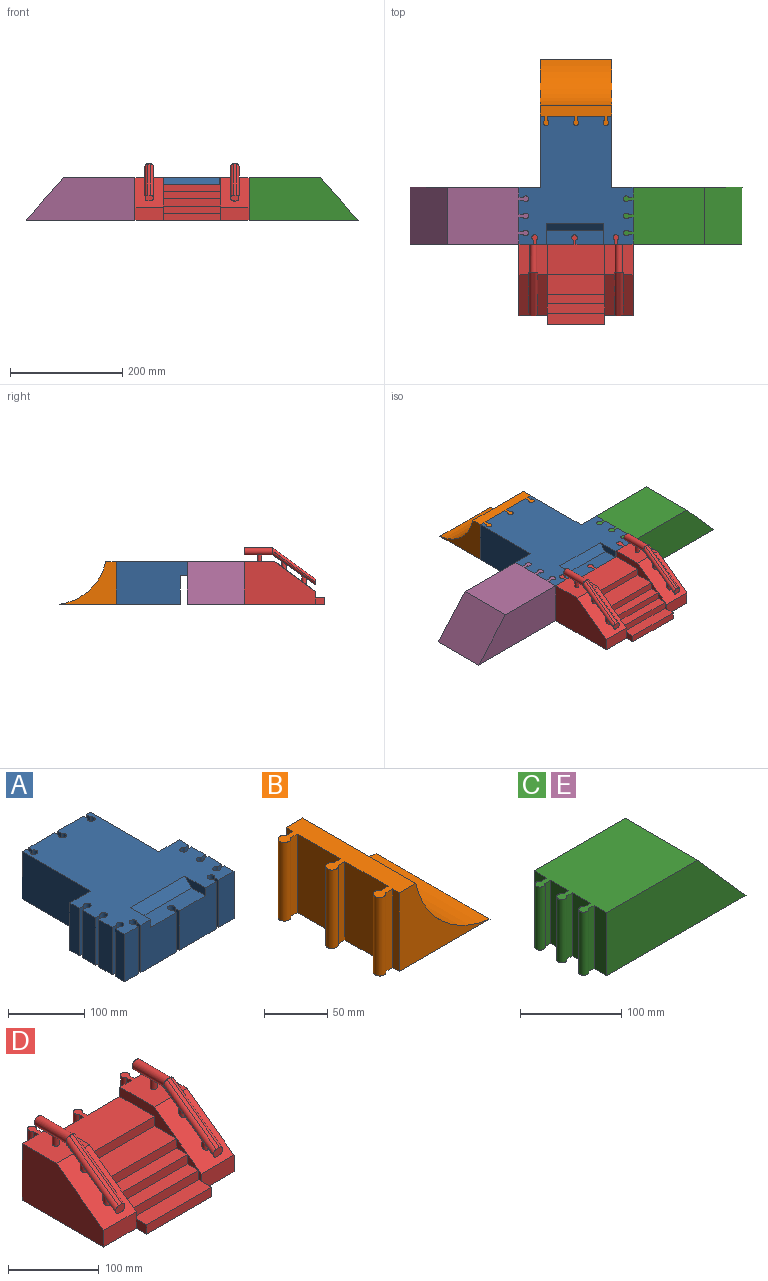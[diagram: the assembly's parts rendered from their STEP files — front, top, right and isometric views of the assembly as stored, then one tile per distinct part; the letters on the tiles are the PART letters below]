
ASSEMBLY  parts=5 mates=4
PART A: 72 faces, bbox 203.2x228.6x76.2 mm
  f0: plane 76.2x68.58mm, normal (0,-1,0), area 4612.9mm2, adj f1,f10,f18,f37,f69,f70
  f1: plane 63.5x7.62mm, normal (-1,0,0), area 483.9mm2, adj f0,f3,f10,f70
  f2: plane 63.5x7.62mm, normal (1,0,0), area 483.9mm2, adj f3,f10,f14,f70
  f3: cylinder r=5.08mm len=63.5mm, axis (0,0,-1), area 1689mm2, adj f1,f2,f10,f70
  f4: plane 76.2x25.4mm, normal (-1,0,0), area 1935.5mm2, adj f10,f18,f53,f57
  f5: plane 76.2x25.4mm, normal (-1,0,0), area 1935.5mm2, adj f10,f18,f50,f54
  f6: plane 76.2x17.78mm, normal (-1,0,0), area 1354.8mm2, adj f10,f11,f18,f51
  f7: plane 76.2x17.78mm, normal (1,0,0), area 1354.8mm2, adj f10,f18,f22,f67
  f8: plane 76.2x25.4mm, normal (1,0,0), area 1935.5mm2, adj f10,f18,f64,f65
  f9: plane 76.2x25.4mm, normal (1,0,0), area 1935.5mm2, adj f10,f18,f61,f62
  f10: plane 203.2x101.6mm, normal (0,0,-1), area 9910.7mm2, adj f0,f1,f2,f3,f4,f5,f6,f7
  f11: plane 76.2x38.1mm, normal (0,1,0), area 2258.1mm2, adj f6,f10,f18,f25,f48,f49
  f12: plane 127x114.3mm, normal (0,0,-1), area 6421.8mm2, adj f15,f16,f17,f23,f24,f25,f26,f27
  f13: plane 76.2x25.4mm, normal (0,-1,0), area 1935.5mm2, adj f10,f18,f19,f40
  f14: plane 76.2x66.04mm, normal (0,-1,0), area 4419.3mm2, adj f2,f10,f18,f39,f68,f70
  f15: plane 76.2x48.26mm, normal (0,1,0), area 3677.4mm2, adj f12,f18,f31,f33
  f16: plane 76.2x48.26mm, normal (0,1,0), area 3677.4mm2, adj f12,f18,f26,f30
  f17: plane 76.2x7.62mm, normal (0,1,0), area 580.6mm2, adj f12,f18,f25,f28
  f18: plane 228.6x203.2mm, normal (0,0,1), area 31611.3mm2, adj f0,f4,f5,f6,f7,f8,f9,f11
  f19: plane 76.2x17.78mm, normal (-1,0,0), area 1354.8mm2, adj f10,f13,f18,f56
  f20: plane 76.2x27.94mm, normal (0,-1,0), area 2129mm2, adj f10,f18,f21,f36
  f21: plane 76.2x17.78mm, normal (1,0,0), area 1354.8mm2, adj f10,f18,f20,f59
  f22: plane 76.2x38.1mm, normal (0,1,0), area 2258.1mm2, adj f7,f10,f18,f23,f46,f49
  f23: plane 127x76.2mm, normal (1,0,0), area 9032.2mm2, adj f12,f18,f22,f24,f45,f49
  f24: plane 76.2x7.62mm, normal (0,1,0), area 580.6mm2, adj f12,f18,f23,f34
  f25: plane 127x76.2mm, normal (-1,0,0), area 9032.2mm2, adj f11,f12,f17,f18,f41,f49
  f26: plane 76.2x7.62mm, normal (-1,0,0), area 580.6mm2, adj f12,f16,f18,f27
  f27: cylinder r=5.08mm len=76.2mm, axis (0,0,-1), area 2026.8mm2, adj f12,f18,f26,f28
  f28: plane 76.2x7.62mm, normal (1,0,0), area 580.6mm2, adj f12,f17,f18,f27
  f29: cylinder r=5.08mm len=76.2mm, axis (0,0,-1), area 2026.8mm2, adj f12,f18,f30,f31
  f30: plane 76.2x7.62mm, normal (1,0,0), area 580.6mm2, adj f12,f16,f18,f29
  f31: plane 76.2x7.62mm, normal (-1,0,0), area 580.6mm2, adj f12,f15,f18,f29
  f32: cylinder r=5.08mm len=76.2mm, axis (0,0,-1), area 2026.8mm2, adj f12,f18,f33,f34
  f33: plane 76.2x7.62mm, normal (1,0,0), area 580.6mm2, adj f12,f15,f18,f32
  f34: plane 76.2x7.62mm, normal (-1,0,0), area 580.6mm2, adj f12,f18,f24,f32
  f35: cylinder r=5.08mm len=76.2mm, axis (0,0,-1), area 2026.8mm2, adj f10,f18,f36,f37
  f36: plane 76.2x7.62mm, normal (-1,0,0), area 580.6mm2, adj f10,f18,f20,f35
  f37: plane 76.2x7.62mm, normal (1,0,0), area 580.6mm2, adj f0,f10,f18,f35
  f38: cylinder r=5.08mm len=76.2mm, axis (0,0,-1), area 2026.8mm2, adj f10,f18,f39,f40
  f39: plane 76.2x7.62mm, normal (-1,0,0), area 580.6mm2, adj f10,f14,f18,f38
  f40: plane 76.2x7.62mm, normal (1,0,0), area 580.6mm2, adj f10,f13,f18,f38
  f41: plane 50.8x12.7mm, normal (0,-1,0), area 645.2mm2, adj f12,f25,f42,f49
  f42: plane 76.2x50.8mm, normal (1,0,0), area 3871mm2, adj f12,f41,f43,f49
  f43: plane 101.6x50.8mm, normal (0,-1,0), area 5161.3mm2, adj f12,f42,f44,f49
  f44: plane 76.2x50.8mm, normal (-1,0,0), area 3871mm2, adj f12,f43,f45,f49
  f45: plane 50.8x12.7mm, normal (0,-1,0), area 645.2mm2, adj f12,f23,f44,f49
  f46: plane 63.5x50.8mm, normal (-1,0,0), area 3225.8mm2, adj f10,f22,f47,f49
  f47: plane 152.4x50.8mm, normal (0,1,0), area 7741.9mm2, adj f10,f46,f48,f49
  f48: plane 63.5x50.8mm, normal (1,0,0), area 3225.8mm2, adj f10,f11,f47,f49
  f49: plane 152.4x152.4mm, normal (0,0,-1), area 19032.2mm2, adj f11,f22,f23,f25,f41,f42,f43,f44
  f50: plane 76.2x7.62mm, normal (0,1,0), area 580.6mm2, adj f5,f10,f18,f52
  f51: plane 76.2x7.62mm, normal (0,-1,0), area 580.6mm2, adj f6,f10,f18,f52
  f52: cylinder r=5.08mm len=76.2mm, axis (0,0,-1), area 2026.8mm2, adj f10,f18,f50,f51
  f53: plane 76.2x7.62mm, normal (0,1,0), area 580.6mm2, adj f4,f10,f18,f55
  f54: plane 76.2x7.62mm, normal (0,-1,0), area 580.6mm2, adj f5,f10,f18,f55
  f55: cylinder r=5.08mm len=76.2mm, axis (0,0,-1), area 2026.8mm2, adj f10,f18,f53,f54
  f56: plane 76.2x7.62mm, normal (0,1,0), area 580.6mm2, adj f10,f18,f19,f58
  f57: plane 76.2x7.62mm, normal (0,-1,0), area 580.6mm2, adj f4,f10,f18,f58
  f58: cylinder r=5.08mm len=76.2mm, axis (0,0,-1), area 2026.8mm2, adj f10,f18,f56,f57
  f59: plane 76.2x7.62mm, normal (0,1,0), area 580.6mm2, adj f10,f18,f21,f60
  f60: cylinder r=5.08mm len=76.2mm, axis (0,0,-1), area 2026.8mm2, adj f10,f18,f59,f61
  f61: plane 76.2x7.62mm, normal (0,-1,0), area 580.6mm2, adj f9,f10,f18,f60
  f62: plane 76.2x7.62mm, normal (0,1,0), area 580.6mm2, adj f9,f10,f18,f63
  f63: cylinder r=5.08mm len=76.2mm, axis (0,0,-1), area 2026.8mm2, adj f10,f18,f62,f64
  f64: plane 76.2x7.62mm, normal (0,-1,0), area 580.6mm2, adj f8,f10,f18,f63
  f65: plane 76.2x7.62mm, normal (0,1,0), area 580.6mm2, adj f8,f10,f18,f66
  f66: cylinder r=5.08mm len=76.2mm, axis (0,0,-1), area 2026.8mm2, adj f10,f18,f65,f67
  f67: plane 76.2x7.62mm, normal (0,-1,0), area 580.6mm2, adj f7,f10,f18,f66
  f68: plane 38.1x12.7mm, normal (1,0,0), area 403.2mm2, adj f14,f18,f70,f71
  f69: plane 38.1x12.7mm, normal (-1,0,0), area 403.2mm2, adj f0,f18,f70,f71
  f70: plane 101.6x25.4mm, normal (0,0,1), area 2463.2mm2, adj f0,f1,f2,f3,f14,f68,f69,f71
  f71: plane 101.6x12.7mm, normal (0,-0.71,0.71), area 1824.8mm2, adj f18,f68,f69,f70
PART B: 18 faces, bbox 118.7x127x76.2 mm
  f0: plane 76.2x48.26mm, normal (-1,0,0), area 3677.4mm2, adj f5,f6,f11,f15
  f1: plane 76.2x7.62mm, normal (-1,0,0), area 580.6mm2, adj f3,f5,f6,f12
  f2: plane 76.2x48.26mm, normal (-1,0,0), area 3677.4mm2, adj f5,f6,f10,f13
  f3: plane 101.6x76.2mm, normal (0,1,0), area 3199mm2, adj f1,f5,f6,f7
  f4: plane 76.2x7.62mm, normal (-1,0,0), area 580.6mm2, adj f5,f6,f8,f16
  f5: plane 127x35.56mm, normal (0,0,1), area 2697.2mm2, adj f0,f1,f2,f3,f4,f7,f8,f9
  f6: plane 127x118.7mm, normal (0,0,-1), area 13255.5mm2, adj f0,f1,f2,f3,f4,f7,f8,f9
  f7: cylinder r=97.6mm len=127mm, axis (0,-1,0), area 15269.8mm2, adj f3,f5,f6,f8
  f8: plane 101.6x76.2mm, normal (0,-1,0), area 3199mm2, adj f4,f5,f6,f7
  f9: cylinder r=5.08mm len=76.2mm, axis (0,0,-1), area 2026.8mm2, adj f5,f6,f10,f11
  f10: plane 76.2x7.62mm, normal (0,1,0), area 580.6mm2, adj f2,f5,f6,f9
  f11: plane 76.2x7.62mm, normal (0,-1,0), area 580.6mm2, adj f0,f5,f6,f9
  f12: plane 76.2x7.62mm, normal (0,1,0), area 580.6mm2, adj f1,f5,f6,f14
  f13: plane 76.2x7.62mm, normal (0,-1,0), area 580.6mm2, adj f2,f5,f6,f14
  f14: cylinder r=5.08mm len=76.2mm, axis (0,0,-1), area 2026.8mm2, adj f5,f6,f12,f13
  f15: plane 76.2x7.62mm, normal (0,1,0), area 580.6mm2, adj f0,f5,f6,f17
  f16: plane 76.2x7.62mm, normal (0,-1,0), area 580.6mm2, adj f4,f5,f6,f17
  f17: cylinder r=5.08mm len=76.2mm, axis (0,0,-1), area 2026.8mm2, adj f5,f6,f15,f16
PART C: 18 faces, bbox 211.3x101.6x76.2 mm
  f0: plane 76.2x25.4mm, normal (-1,0,0), area 1935.5mm2, adj f6,f7,f14,f17
  f1: plane 76.2x25.4mm, normal (-1,0,0), area 1935.5mm2, adj f6,f7,f9,f13
  f2: plane 76.2x17.78mm, normal (-1,0,0), area 1354.8mm2, adj f5,f6,f7,f11
  f3: plane 76.2x17.78mm, normal (-1,0,0), area 1354.8mm2, adj f4,f6,f7,f15
  f4: plane 194.2x76.2mm, normal (0,-1,0), area 12237.8mm2, adj f3,f6,f7,f8
  f5: plane 194.2x76.2mm, normal (0,1,0), area 12237.8mm2, adj f2,f6,f7,f8
  f6: plane 144.1x101.6mm, normal (0,0,1), area 13255.5mm2, adj f0,f1,f2,f3,f4,f5,f8,f9
  f7: plane 211.3x101.6mm, normal (0,0,-1), area 20083.3mm2, adj f0,f1,f2,f3,f4,f5,f8,f9
  f8: plane 101.6x76.2mm, normal (0.75,0,0.66), area 10322.6mm2, adj f4,f5,f6,f7
  f9: plane 76.2x7.62mm, normal (0,-1,0), area 580.6mm2, adj f1,f6,f7,f10
  f10: cylinder r=5.08mm len=76.2mm, axis (0,0,-1), area 2026.8mm2, adj f6,f7,f9,f11
  f11: plane 76.2x7.62mm, normal (0,1,0), area 580.6mm2, adj f2,f6,f7,f10
  f12: cylinder r=5.08mm len=76.2mm, axis (0,0,-1), area 2026.8mm2, adj f6,f7,f13,f14
  f13: plane 76.2x7.62mm, normal (0,1,0), area 580.6mm2, adj f1,f6,f7,f12
  f14: plane 76.2x7.62mm, normal (0,-1,0), area 580.6mm2, adj f0,f6,f7,f12
  f15: plane 76.2x7.62mm, normal (0,-1,0), area 580.6mm2, adj f3,f6,f7,f16
  f16: cylinder r=5.08mm len=76.2mm, axis (0,0,-1), area 2026.8mm2, adj f6,f7,f15,f17
  f17: plane 76.2x7.62mm, normal (0,1,0), area 580.6mm2, adj f0,f6,f7,f16
PART D: 83 faces, bbox 207.1x164.2x104.6 mm
  f0: plane 63.5x7.62mm, normal (1,0,0), area 483.9mm2, adj f1,f2,f3,f4
  f1: plane 101.6x71.17mm, normal (0,0,1), area 5610.8mm2, adj f0,f2,f4,f5,f6,f7,f8,f9
  f2: plane 76.2x68.58mm, normal (0,1,0), area 4580.6mm2, adj f0,f1,f3,f6,f10,f11
  f3: plane 203.2x160.35mm, normal (0,0,-1), area 27810.1mm2, adj f0,f2,f4,f7,f8,f11,f12,f13
  f4: cylinder r=5.08mm len=63.5mm, axis (0,0,-1), area 1689mm2, adj f0,f1,f3,f7
  f5: plane 101.6x12.7mm, normal (0,-1,0), area 1290.3mm2, adj f1,f6,f9,f26
  f6: plane 88.43x25.4mm, normal (-1,0,0), area 1121.2mm2, adj f1,f2,f5,f10,f26,f27
  f7: plane 63.5x7.62mm, normal (-1,0,0), area 483.9mm2, adj f1,f3,f4,f8
  f8: plane 76.2x66.04mm, normal (0,1,0), area 4451.6mm2, adj f1,f3,f7,f9,f21,f28
  f9: plane 88.43x25.4mm, normal (1,0,0), area 1121.2mm2, adj f1,f5,f8,f26,f28,f29
  f10: plane 71.03x50.8mm, normal (0,0,1), area 2811.3mm2, adj f2,f6,f11,f22,f23,f24,f25,f27
  f11: plane 76.2x7.62mm, normal (-1,0,0), area 580.6mm2, adj f2,f3,f10,f22
  f12: plane 50.8x22.41mm, normal (0,-1,0), area 1138.2mm2, adj f3,f13,f25,f27,f31
  f13: plane 16.25x12.7mm, normal (1,0,0), area 206.4mm2, adj f3,f12,f14,f32
  f14: plane 101.6x12.7mm, normal (0,-1,0), area 1290.3mm2, adj f3,f13,f15,f32
  f15: plane 16.25x12.7mm, normal (-1,0,0), area 206.4mm2, adj f3,f14,f16,f32
  f16: plane 50.8x22.41mm, normal (0,-1,0), area 1138.2mm2, adj f3,f15,f17,f29,f33
  f17: plane 127x76.2mm, normal (-1,0,0), area 7711.9mm2, adj f3,f16,f18,f28,f29
  f18: plane 76.2x25.4mm, normal (0,1,0), area 1935.5mm2, adj f3,f17,f19,f28
  f19: plane 76.2x7.62mm, normal (-1,0,0), area 580.6mm2, adj f3,f18,f20,f28
  f20: cylinder r=5.08mm len=76.2mm, axis (0,0,-1), area 2026.8mm2, adj f3,f19,f21,f28
  f21: plane 76.2x7.62mm, normal (1,0,0), area 580.6mm2, adj f3,f8,f20,f28
  f22: cylinder r=5.08mm len=76.2mm, axis (0,0,-1), area 2026.8mm2, adj f3,f10,f11,f23
  f23: plane 76.2x7.62mm, normal (1,0,0), area 580.6mm2, adj f3,f10,f22,f24
  f24: plane 76.2x27.94mm, normal (0,1,0), area 2129mm2, adj f3,f10,f23,f25
  f25: plane 127x76.2mm, normal (1,0,0), area 7711.9mm2, adj f3,f10,f12,f24,f27
  f26: plane 101.6x34.36mm, normal (0,0,1), area 3491mm2, adj f5,f6,f9,f34
  f27: plane 76.93x57.65mm, normal (0,-0.59,0.81), area 4496.3mm2, adj f6,f10,f12,f25,f31,f35,f36,f37
  f28: plane 71.03x50.8mm, normal (0,0,1), area 2811.3mm2, adj f8,f9,f17,f18,f19,f20,f21,f29
  f29: plane 73.66x54.38mm, normal (0,-0.59,0.81), area 4496.3mm2, adj f9,f16,f17,f28,f33,f40,f41,f42
  f30: cylinder r=3.81mm len=12.7mm, axis (0,0,-1), area 304mm2, adj f10,f44,f45,f46
  f31: plane 12.7x4.07mm, normal (-1,0,0), area 45.6mm2, adj f12,f27,f32,f47
  f32: plane 101.6x20.32mm, normal (0,0,1), area 2064.5mm2, adj f13,f14,f15,f31,f33,f47
  f33: plane 12.7x4.07mm, normal (1,0,0), area 45.6mm2, adj f16,f29,f32,f47
  f34: plane 101.6x12.7mm, normal (0,-1,0), area 1290.3mm2, adj f26,f38,f43,f48
  f35: cylinder r=3.81mm len=16.79mm, axis (0,0,1), area 276.3mm2, adj f27,f49,f50,f51,f52,f53
  f36: cylinder r=3.81mm len=14.19mm, axis (0,0,1), area 233.8mm2, adj f27,f50,f51,f53,f54
  f37: plane 17.25x12.7mm, normal (-1,0,0), area 109.5mm2, adj f27,f55,f56
  f38: plane 17.25x12.7mm, normal (-1,0,0), area 109.5mm2, adj f27,f34,f48
  f39: cylinder r=3.81mm len=12.7mm, axis (0,0,-1), area 286.5mm2, adj f28,f57,f58
  f40: cylinder r=3.81mm len=15.86mm, axis (0,0,1), area 274.3mm2, adj f29,f59,f60,f61,f62
  f41: cylinder r=3.81mm len=14.92mm, axis (0,0,1), area 240.4mm2, adj f29,f59,f61,f63,f64,f65
  f42: plane 17.25x12.7mm, normal (1,0,0), area 109.5mm2, adj f29,f55,f56
  f43: plane 17.25x12.7mm, normal (1,0,0), area 109.5mm2, adj f29,f34,f48
  f44: plane 4.15x0.61mm, normal (0,0,1), area 1.7mm2, adj f30,f45
  f45: cylinder r=6.35mm len=50.8mm, axis (0,-1,0), area 1982.9mm2, adj f30,f44,f46,f66,f67
  f46: plane 4.14x0.61mm, normal (0,0,1), area 1.7mm2, adj f30,f45
  f47: plane 101.6x12.7mm, normal (0,-1,0), area 1290.3mm2, adj f31,f32,f33,f56
  f48: plane 101.6x17.25mm, normal (0,0,1), area 1752.8mm2, adj f34,f38,f43,f55
  f49: plane 17.22x11.98mm, normal (0,0.57,-0.82), area 102.4mm2, adj f35,f50,f53,f68
  f50: cylinder r=5.08mm len=82.47mm, axis (0,-0.82,-0.57), area 699.7mm2, adj f35,f36,f49,f51,f54,f68,f69,f70
  f51: plane 31.57x22.38mm, normal (0,0.57,-0.82), area 179.7mm2, adj f35,f36,f50,f52,f53
  f52: plane 3.19x0.35mm, normal (0,0,1), area 0.8mm2, adj f35,f51
  f53: cylinder r=5.08mm len=82.47mm, axis (0,0.82,0.57), area 699.7mm2, adj f35,f36,f49,f51,f54,f68,f71,f72
  f54: plane 19.22x13.79mm, normal (0,0.57,-0.82), area 106.5mm2, adj f36,f50,f53,f71
  f55: plane 101.6x12.7mm, normal (0,-1,0), area 1290.3mm2, adj f37,f42,f48,f56
  f56: plane 101.6x17.25mm, normal (0,0,1), area 1752.8mm2, adj f37,f42,f47,f55
  f57: plane 3.67x0.47mm, normal (0,0,1), area 1.2mm2, adj f39,f58
  f58: cylinder r=6.35mm len=50.81mm, axis (0,-1,0), area 1979.8mm2, adj f39,f57,f64,f74,f75
  f59: cylinder r=5.08mm len=82.47mm, axis (0,0.82,0.57), area 699mm2, adj f40,f41,f60,f62,f63,f64,f74,f76
  f60: plane 19.85x14.23mm, normal (0,0.57,-0.82), area 110.4mm2, adj f40,f59,f61,f78
  f61: cylinder r=5.08mm len=82.47mm, axis (0,-0.82,-0.57), area 699mm2, adj f40,f41,f60,f62,f63,f64,f74,f78
  f62: plane 6.38x1.73mm, normal (0,0,1), area 7.2mm2, adj f40,f59,f61,f63
  f63: plane 30.74x21.4mm, normal (0,0.57,-0.82), area 186.2mm2, adj f41,f59,f61,f62
  f64: plane 16.74x11.65mm, normal (0,0.57,-0.82), area 103.1mm2, adj f41,f58,f59,f61,f65,f74
  f65: plane 4.91x0.9mm, normal (0,0,1), area 3mm2, adj f41,f64
  f66: plane 12.71x12.71mm, normal (0,-1,0), area 126.7mm2, adj f45
  f67: plane 12.7x12.7mm, normal (0,1,0), area 126.7mm2, adj f45
  f68: plane 16.43x11.64mm, normal (0,-1,0), area 129.9mm2, adj f49,f50,f53,f69,f73,f81
  f69: cylinder r=5.08mm len=82.14mm, axis (0,0.81,0.59), area 721.8mm2, adj f50,f68,f70,f71,f81
  f70: plane 13.51x9.87mm, normal (-1,0,0), area 3.1mm2, adj f50,f69,f71
  f71: plane 16.8x14.51mm, normal (0,1,0), area 170.1mm2, adj f50,f53,f54,f69,f70,f72,f73,f81
  f72: plane 13.51x9.87mm, normal (1,0,0), area 3.1mm2, adj f53,f71,f73
  f73: cylinder r=5.08mm len=82.14mm, axis (0,-0.81,-0.59), area 721.8mm2, adj f53,f68,f71,f72,f81
  f74: plane 16.8x14.5mm, normal (0,1,0), area 43.3mm2, adj f58,f59,f61,f64,f76,f77,f79,f80
  f75: plane 12.7x12.7mm, normal (0,1,0), area 126.7mm2, adj f58
  f76: plane 13.37x9.77mm, normal (1,0,0), area 3.1mm2, adj f59,f74,f77
  f77: cylinder r=5.08mm len=82.14mm, axis (0,-0.81,-0.59), area 721.7mm2, adj f59,f74,f76,f78,f82
  f78: plane 16.43x11.64mm, normal (0,-1,0), area 129.9mm2, adj f59,f60,f61,f77,f79,f82
  f79: cylinder r=5.08mm len=82.14mm, axis (0,0.81,0.59), area 721.7mm2, adj f61,f74,f78,f80,f82
  f80: plane 13.37x9.77mm, normal (-1,0,0), area 3.1mm2, adj f61,f74,f79
  f81: plane 76.67x56mm, normal (0,-0.59,0.81), area 482.3mm2, adj f68,f69,f71,f73
  f82: plane 76.67x56mm, normal (0,-0.59,0.81), area 482.3mm2, adj f74,f77,f78,f79
PART E: same geometry as C
PLACE A t=(-178.03,18.18,43.23)mm fixed
PLACE B rot(axis=(0,0,1),90deg) t=(-186.53,248.93,43.23)mm
PLACE C rot(axis=(0.68,-0.44,-0.59),0deg) t=(-32.2,16.89,43.23)mm
PLACE D t=(-177.76,-109.24,43.23)mm
PLACE E rot(axis=(0,0,1),180deg) t=(-317.95,-13.34,43.23)mm
MATE slider A.f18 <-> C.f6  axis (0,0,1) through (-73.48,-31.25,119.43)mm
MATE slider A.f18 <-> D.f28  axis (0,0,1) through (-246.2,-49.03,119.43)mm
MATE slider A.f18 <-> E.f6  axis (0,0,1) through (-276.68,29.71,119.43)mm
MATE slider A.f18 <-> B.f5  axis (0,0,1) through (-225.88,171.95,119.43)mm
